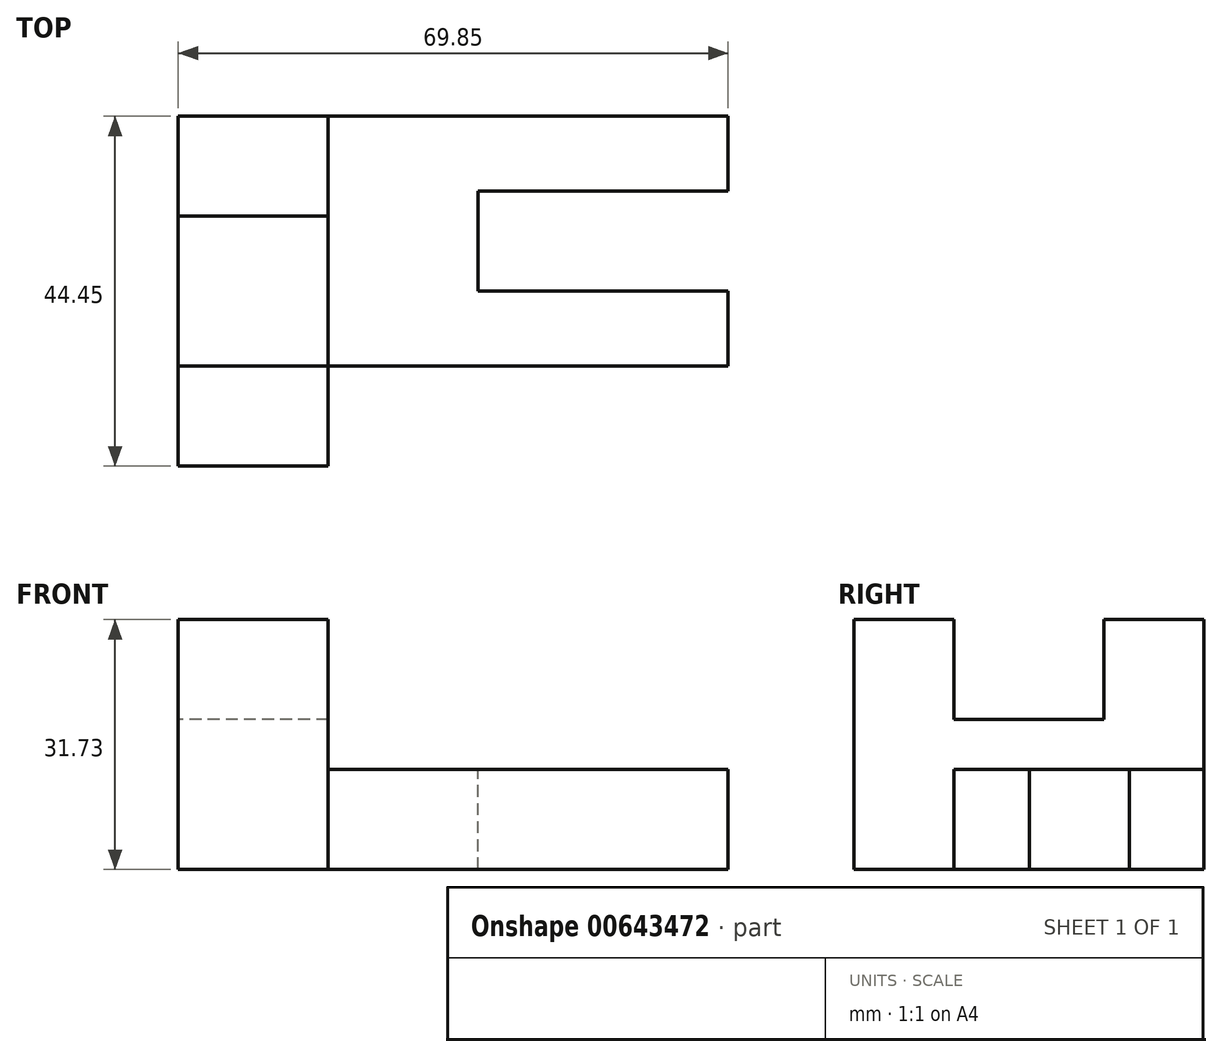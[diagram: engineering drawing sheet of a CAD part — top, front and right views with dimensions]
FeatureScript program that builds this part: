
annotation { "Feature Type Name" : "Feature", "Feature Type Description" : "" }
export const myFeature = defineFeature(function(context is Context, id is Id, definition is map)
    precondition{}
    {
        {
            var Q0;
            Q0=qCreatedBy(makeId("Right.planeOp"),FACE);
            var sketch = newSketch(context, id + "F0", { "sketchPlane" : qUnion([Q0])});
            skLineSegment(sketch, "E0", {"start": v(0, 0) * mm, "end": v(44.45, 0) * mm});
            skLineSegment(sketch, "E1", {"start": v(0, 0) * mm, "end": v(0, 31.73) * mm});
            skLineSegment(sketch, "E2", {"start": v(0, 31.73) * mm, "end": v(12.68, 31.73) * mm});
            skLineSegment(sketch, "E3", {"start": v(12.68, 31.73) * mm, "end": v(12.68, 19.03) * mm});
            skLineSegment(sketch, "E4", {"start": v(12.68, 19.03) * mm, "end": v(31.75, 19.03) * mm});
            skLineSegment(sketch, "E5", {"start": v(31.75, 19.03) * mm, "end": v(31.75, 31.73) * mm});
            skLineSegment(sketch, "E6", {"start": v(31.75, 31.73) * mm, "end": v(44.45, 31.73) * mm});
            skLineSegment(sketch, "E7", {"start": v(44.45, 31.73) * mm, "end": v(44.45, 0) * mm});
            skSolve(sketch);
        }
        {
            var Q0;
            Q0=makeQuery(id+"F0.imprint","IMPRINT",FACE,{"disambiguationData":[TD([[makeQuery(id+"F0.imprint","IMPRINT",EDGE,{"derivedFrom":sQuery(id+"F0.wireOp",EDGE,"E0")}),1.0]])]});
            extrude(context, id + "F1", {"entities" : qUnion([Q0]), "depth" : 19.05 * mm, "offsetDistance" : 25.4 * mm});
        }
        {
            var Q0;
            Q0=makeQuery(id+"F1.opExtrude","CAP_FACE",FACE,{"disambiguationData":[OSD([sQuery(id+"F0.wireOp",EDGE,"E0"),sQuery(id+"F0.wireOp",EDGE,"E1"),sQuery(id+"F0.wireOp",EDGE,"E2"),sQuery(id+"F0.wireOp",EDGE,"E3"),sQuery(id+"F0.wireOp",EDGE,"E4"),sQuery(id+"F0.wireOp",EDGE,"E5"),sQuery(id+"F0.wireOp",EDGE,"E6"),sQuery(id+"F0.wireOp",EDGE,"E7")])],"isStart":false});
            var sketch = newSketch(context, id + "F2", { "sketchPlane" : qUnion([Q0])});
            skLineSegment(sketch, "E8", {"start": v(12.71, 0) * mm, "end": v(12.71, 12.7) * mm});
            skLineSegment(sketch, "E9", {"start": v(12.71, 12.7) * mm, "end": v(44.45, 12.7) * mm});
            skLineSegment(sketch, "E10", {"start": v(44.45, 12.7) * mm, "end": v(44.45, 0) * mm});
            skLineSegment(sketch, "E11", {"start": v(44.45, 0) * mm, "end": v(12.71, 0) * mm});
            skSolve(sketch);
        }
        {
            var Q0;
            Q0 = qSketchRegion(id + "F2", true);
            extrude(context, id + "F3", {"entities" : qUnion([Q0]), "operationType" : NewBodyOperationType.ADD, "depth" : 50.8 * mm, "offsetDistance" : 25.4 * mm});
        }
        {
            var Q0;
            Q0=makeQuery(id+"F3.opExtrude","SWEPT_FACE",FACE,{"disambiguationData":[OSD([sQuery(id+"F2.wireOp",EDGE,"E9")])]});
            var sketch = newSketch(context, id + "F4", { "sketchPlane" : qUnion([Q0])});
            skLineSegment(sketch, "E12", {"start": v(69.85, 12.71) * mm, "end": v(69.85, 22.24) * mm});
            skLineSegment(sketch, "E13", {"start": v(69.85, 22.24) * mm, "end": v(38.1, 22.24) * mm});
            skLineSegment(sketch, "E14", {"start": v(38.1, 22.24) * mm, "end": v(38.1, 34.95) * mm});
            skLineSegment(sketch, "E15", {"start": v(38.1, 34.95) * mm, "end": v(69.85, 34.95) * mm});
            skLineSegment(sketch, "E16", {"start": v(69.85, 34.95) * mm, "end": v(69.85, 22.24) * mm});
            skSolve(sketch);
        }
        {
            var Q0;
            Q0=makeQuery(id+"F4.imprint","IMPRINT",FACE,{"disambiguationData":[TD([[makeQuery(id+"F4.imprint","IMPRINT",EDGE,{"derivedFrom":sQuery(id+"F4.wireOp",EDGE,"E13")}),-1.0]])]});
            extrude(context, id + "F5", {"entities" : qUnion([Q0]), "operationType" : NewBodyOperationType.REMOVE, "oppositeDirection" : true, "depth" : 25.4 * mm, "offsetDistance" : 25.4 * mm});
        }
    });
